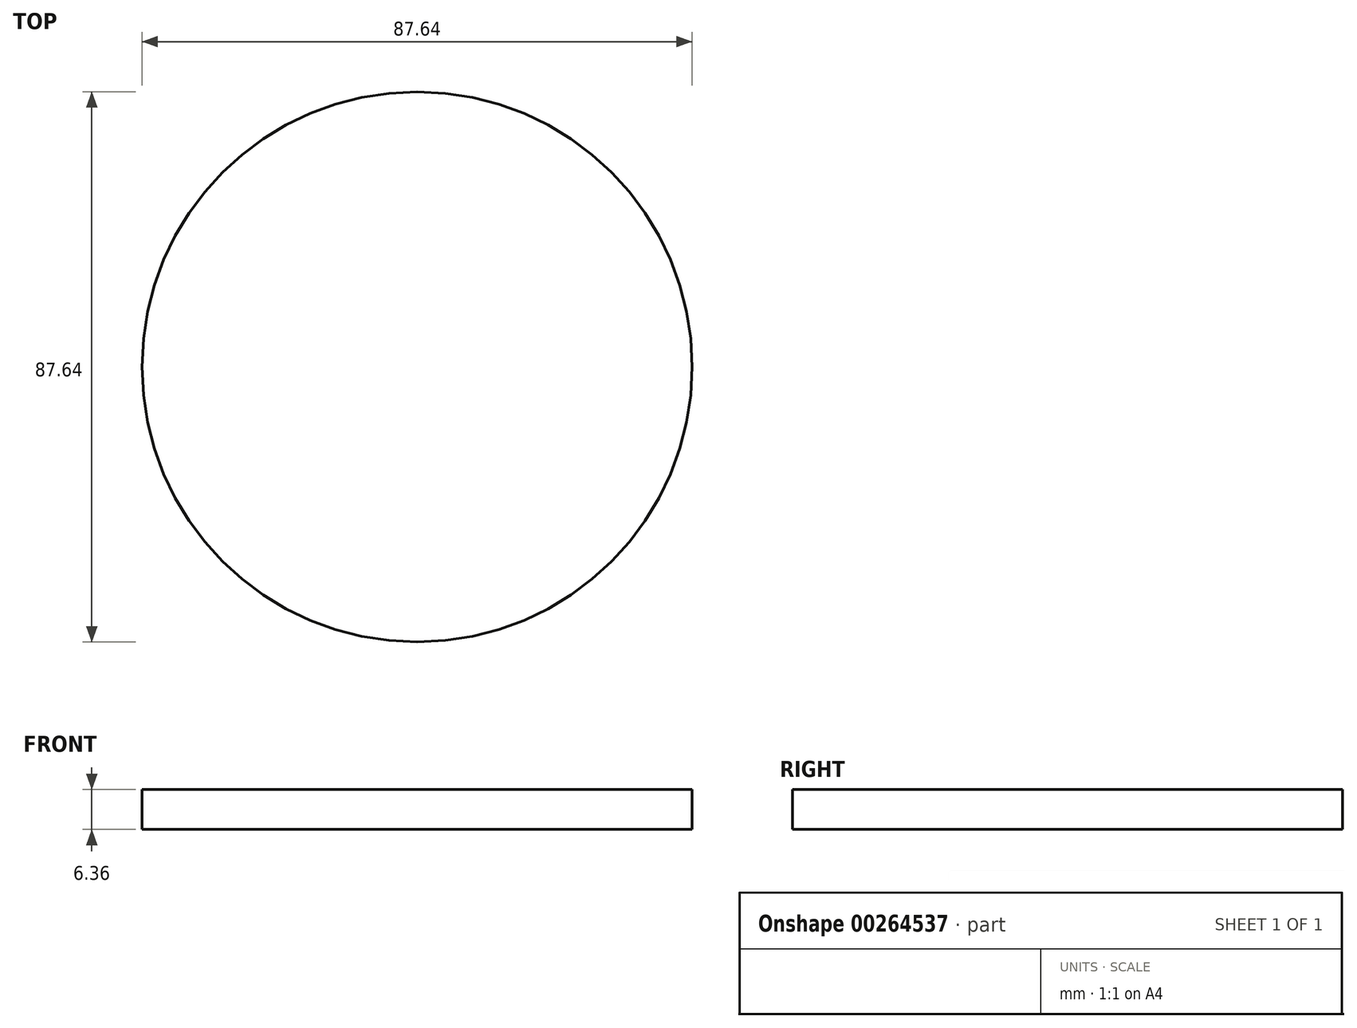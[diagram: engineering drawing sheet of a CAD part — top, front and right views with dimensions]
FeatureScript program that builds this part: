
annotation { "Feature Type Name" : "Feature", "Feature Type Description" : "" }
export const myFeature = defineFeature(function(context is Context, id is Id, definition is map)
    precondition{}
    {
        {
            var Q0;
            Q0=qCreatedBy(makeId("Top.planeOp"),FACE);
            var sketch = newSketch(context, id + "F0", { "sketchPlane" : qUnion([Q0])});
            skCircle(sketch, "E0", {"center": v(0, 0) * mm, "radius": 43.82 * mm});
            skSolve(sketch);
        }
        {
            var Q0;
            Q0=makeQuery(id+"F0.imprint","IMPRINT",FACE,{"disambiguationData":[TD([[makeQuery(id+"F0.imprint","IMPRINT",EDGE,{"derivedFrom":sQuery(id+"F0.wireOp",EDGE,"E0")}),1.0]])]});
            extrude(context, id + "F1", {"entities" : qUnion([Q0]), "depth" : 6.35 * mm, "symmetric" : true});
        }
    });
